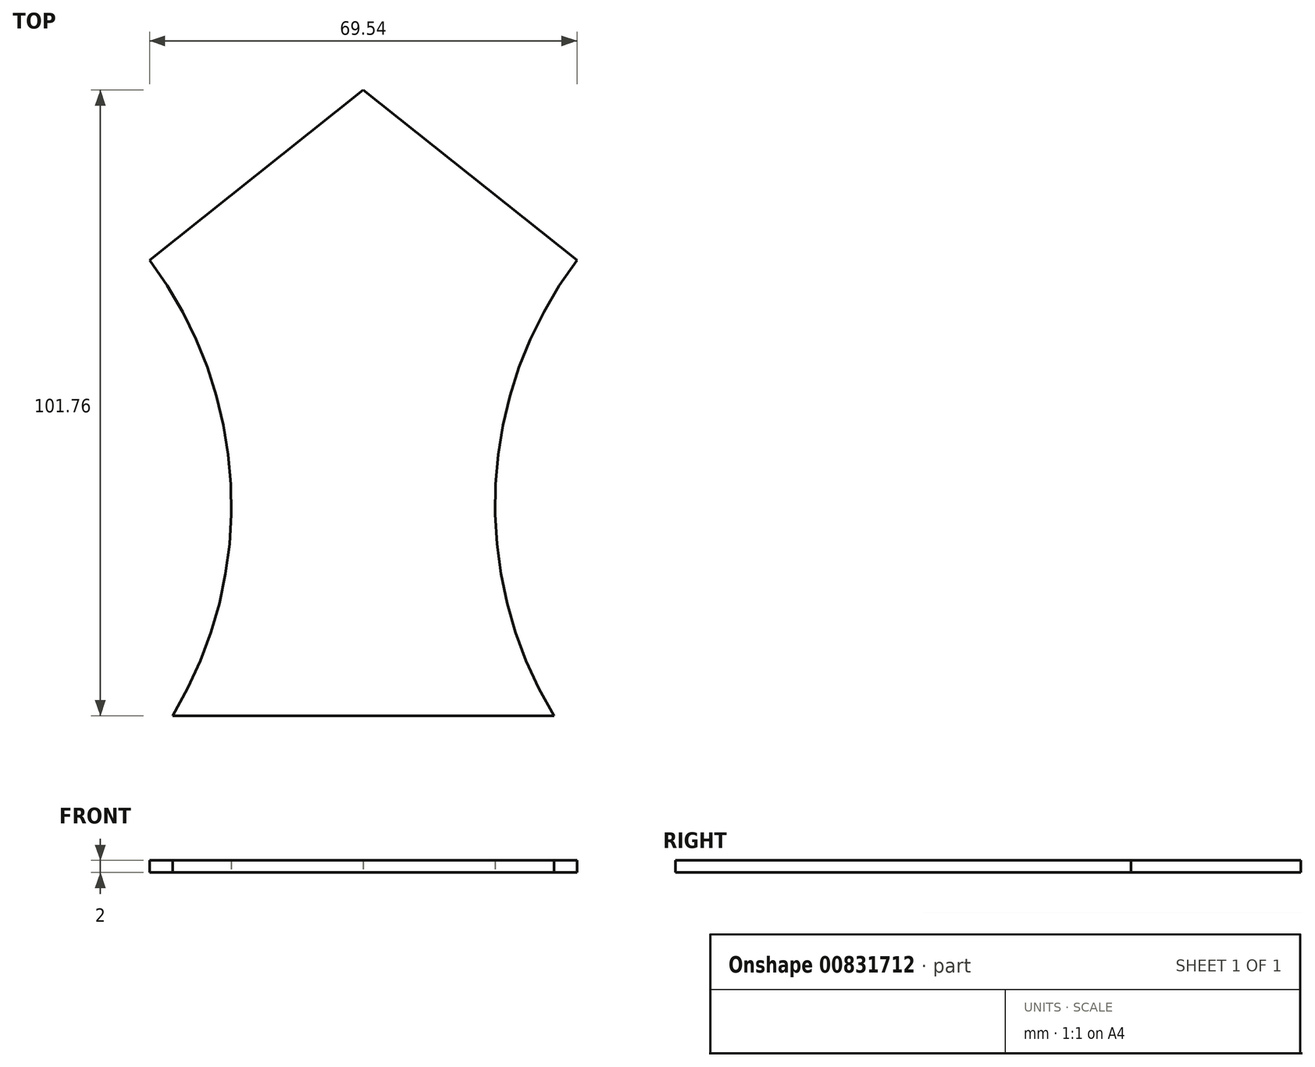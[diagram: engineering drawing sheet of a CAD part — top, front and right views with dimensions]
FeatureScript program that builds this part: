
annotation { "Feature Type Name" : "Feature", "Feature Type Description" : "" }
export const myFeature = defineFeature(function(context is Context, id is Id, definition is map)
    precondition{}
    {
        {
            var Q0;
            Q0=qCreatedBy(makeId("Top.planeOp"),FACE);
            var sketch = newSketch(context, id + "F0", { "sketchPlane" : qUnion([Q0])});
            skArc(sketch, "E0", {"start": v(-31.01, -25.37) * mm, "mid": v(-21.53, 12.26) * mm, "end": v(-34.77, 48.73) * mm});
            skLineSegment(sketch, "E1", {"start": v(0, 58.4) * mm, "end": v(0, -37.72) * mm});
            skArc(sketch, "E2.MirrorCS", {"start": v(31.01, -25.37) * mm, "mid": v(21.53, 12.26) * mm, "end": v(34.77, 48.73) * mm});
            skLineSegment(sketch, "E3", {"start": v(-31.01, -25.37) * mm, "end": v(31.01, -25.37) * mm});
            skLineSegment(sketch, "E4", {"start": v(-34.77, 48.73) * mm, "end": v(0, 76.39) * mm});
            skLineSegment(sketch, "E5", {"start": v(0, 76.39) * mm, "end": v(34.77, 48.73) * mm});
            skSolve(sketch);
        }
        {
            var Q0;
            Q0 = qSketchRegion(id + "F0", true);
            extrude(context, id + "F1", {"entities" : qUnion([Q0]), "depth" : 2 * mm, "offsetDistance" : 25.4 * mm});
        }
    });
